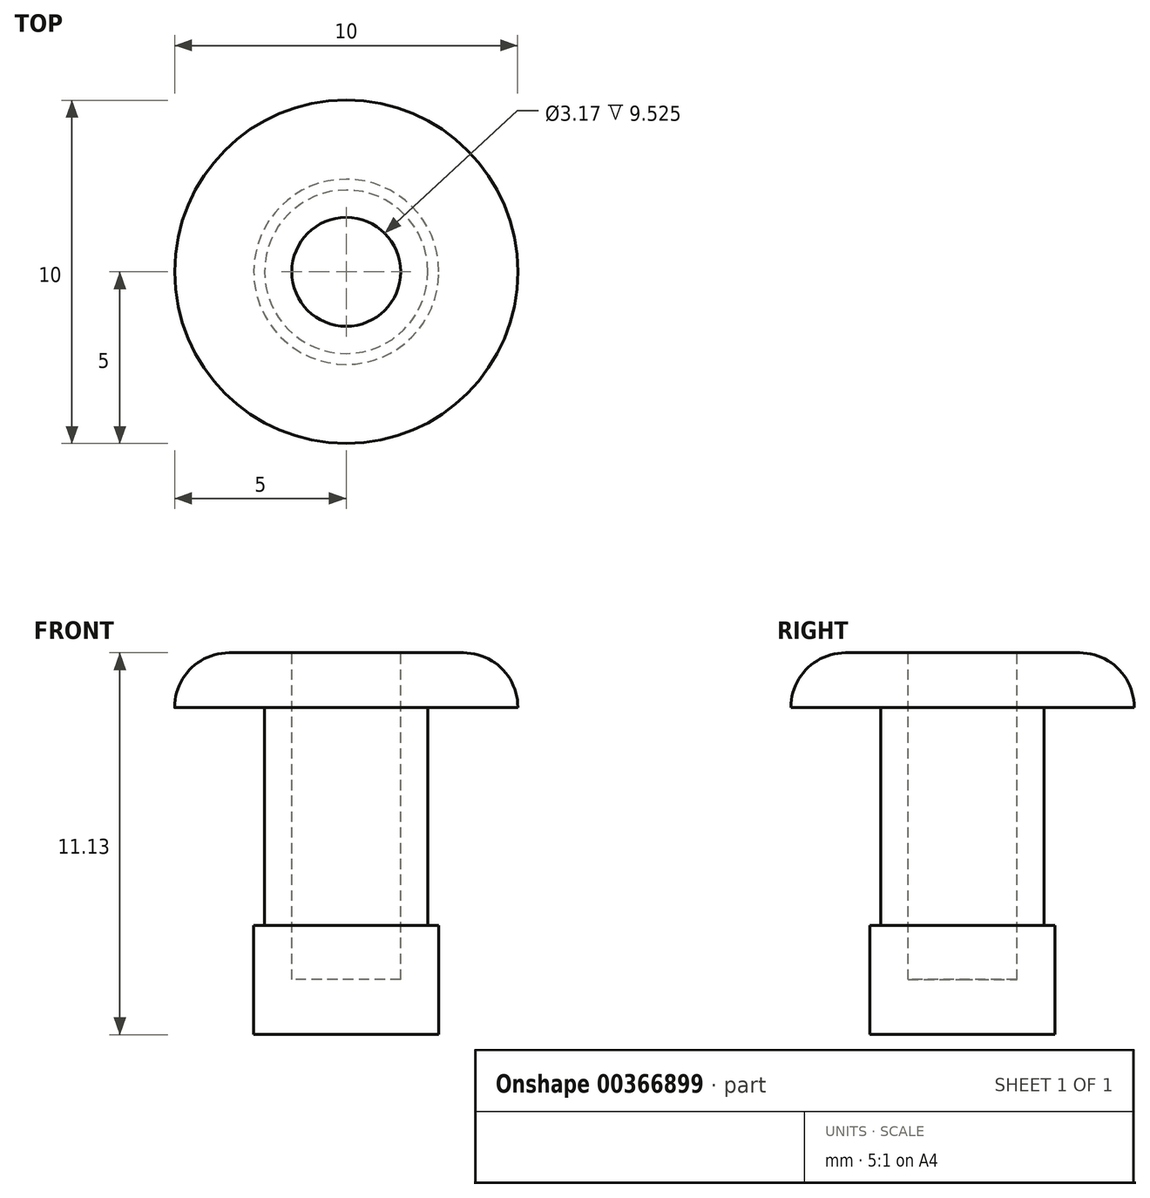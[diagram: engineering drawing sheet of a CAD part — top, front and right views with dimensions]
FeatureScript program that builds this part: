
annotation { "Feature Type Name" : "Feature", "Feature Type Description" : "" }
export const myFeature = defineFeature(function(context is Context, id is Id, definition is map)
    precondition{}
    {
        {
            var Q0;
            Q0=qCreatedBy(makeId("Front.planeOp"),FACE);
            var sketch = newSketch(context, id + "F0", { "sketchPlane" : qUnion([Q0]) });
            skLineSegment(sketch, "E0", {"start": v(0, 0) * mm, "end": v(5, 0) * mm});
            skLineSegment(sketch, "E1", {"start": v(5, 0) * mm, "end": v(5, -1.6) * mm});
            skLineSegment(sketch, "E2", {"start": v(5, -1.6) * mm, "end": v(2.38, -1.6) * mm});
            skLineSegment(sketch, "E3", {"start": v(2.38, -1.6) * mm, "end": v(2.38, -11.13) * mm, "construction": true});
            skLineSegment(sketch, "E4", {"start": v(2.38, -11.13) * mm, "end": v(0, -11.13) * mm});
            skLineSegment(sketch, "E5", {"start": v(0, -11.13) * mm, "end": v(0, 0) * mm});
            skLineSegment(sketch, "E6", {"start": v(2.38, -11.13) * mm, "end": v(2.7, -11.13) * mm});
            skLineSegment(sketch, "E7", {"start": v(2.7, -11.13) * mm, "end": v(2.7, -7.95) * mm});
            skLineSegment(sketch, "E8", {"start": v(2.7, -7.95) * mm, "end": v(2.38, -7.95) * mm});
            skLineSegment(sketch, "E9", {"start": v(2.38, -7.95) * mm, "end": v(2.38, -1.6) * mm});
            skSolve(sketch);
        }
        {
            var Q0;
            Q0=makeQuery(id+"F0.imprint","IMPRINT",FACE,{"disambiguationData":[TD([[makeQuery(id+"F0.imprint","IMPRINT",EDGE,{"derivedFrom":sQuery(id+"F0.wireOp",EDGE,"E0")}),-1.0]])]});
            var Q1;
            Q1=sQuery(id+"F0.wireOp",EDGE,"E5");
            revolve(context, id + "F1", {"entities" : qUnion([Q0]), "axis" : qUnion([Q1]), "revolveType" : RevolveType.FULL});
        }
        {
            var Q0;
            Q0=makeQuery(id+"F1.opRevolve","SWEPT_FACE",FACE,{"disambiguationData":[OSD([sQuery(id+"F0.wireOp",EDGE,"E0")])]});
            var sketch = newSketch(context, id + "F2", { "sketchPlane" : qUnion([Q0]) });
            skCircle(sketch, "E10", {"center": v(0, 0) * mm, "radius": 1.59 * mm});
            skSolve(sketch);
        }
        {
            var Q0;
            Q0=makeQuery(id+"F2.imprint","IMPRINT",FACE,{"disambiguationData":[TD([[makeQuery(id+"F2.imprint","IMPRINT",EDGE,{"derivedFrom":sQuery(id+"F2.wireOp",EDGE,"E10")}),1.0]])]});
            extrude(context, id + "F3", {"entities" : qUnion([Q0]), "operationType" : NewBodyOperationType.REMOVE, "oppositeDirection" : true, "depth" : 9.52 * mm});
        }
        {
            var Q0;
            Q0=makeQuery(id+"F1.opRevolve","SWEPT_EDGE",EDGE,{"disambiguationData":[OSD([sQuery(id+"F0.wireOp",EDGE,"E0"),sQuery(id+"F0.wireOp",EDGE,"E1")])]});
            fillet(context, id + "F4", {"entities" : qUnion([Q0]), "radius" : 1.59 * mm, "tangentPropagation" : true, "conicFillet" : false});
        }
        {
            var Q0;
            Q0=makeQuery(id+"F1.opRevolve","SWEPT_BODY",BODY,{"disambiguationData":[OSD([sQuery(id+"F0.wireOp",EDGE,"E0"),sQuery(id+"F0.wireOp",EDGE,"E1"),sQuery(id+"F0.wireOp",EDGE,"E2"),sQuery(id+"F0.wireOp",EDGE,"E4"),sQuery(id+"F0.wireOp",EDGE,"E5"),sQuery(id+"F0.wireOp",EDGE,"E6"),sQuery(id+"F0.wireOp",EDGE,"E7"),sQuery(id+"F0.wireOp",EDGE,"E8"),sQuery(id+"F0.wireOp",EDGE,"E9")])]});
            var Q1;
            Q1=qCreatedBy(makeId("Origin.pointOp"),VERTEX);
            var Q2;
            Q2=qCreatedBy(makeId("Top.planeOp"),FACE);
            transform(context, id + "F5", {"entities" : qUnion([Q0]), "transformType" : TransformType.TRANSLATION_DISTANCE, "transformDirection" : qUnion([Q2]), "distance" : 1.59 * mm, "makeCopy" : false});
        }
    });
